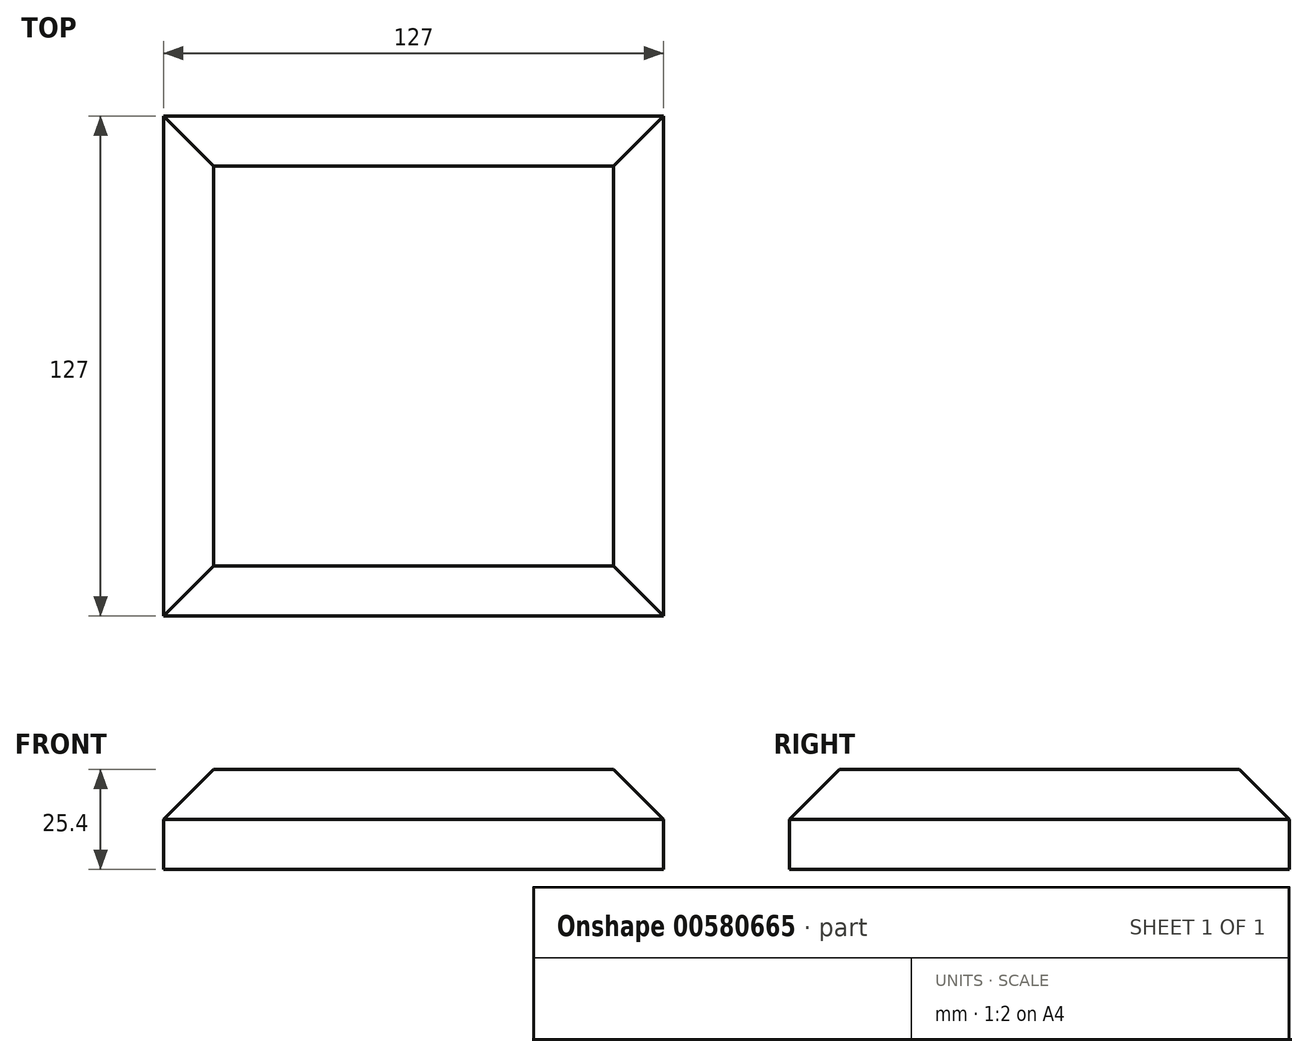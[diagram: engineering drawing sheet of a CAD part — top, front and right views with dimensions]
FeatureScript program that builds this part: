
annotation { "Feature Type Name" : "Feature", "Feature Type Description" : "" }
export const myFeature = defineFeature(function(context is Context, id is Id, definition is map)
    precondition{}
    {
        {
            var Q0;
            Q0=qCreatedBy(makeId("Top.planeOp"),FACE);
            var sketch = newSketch(context, id + "F0", { "sketchPlane" : qUnion([Q0])});
            skLineSegment(sketch, "E0.bottom", {"start": v(63.5, -63.5) * mm, "end": v(-63.5, -63.5) * mm});
            skLineSegment(sketch, "E0.top", {"start": v(63.5, 63.5) * mm, "end": v(-63.5, 63.5) * mm});
            skLineSegment(sketch, "E0.left", {"start": v(63.5, -63.5) * mm, "end": v(63.5, 63.5) * mm});
            skLineSegment(sketch, "E0.right", {"start": v(-63.5, -63.5) * mm, "end": v(-63.5, 63.5) * mm});
            skPoint(sketch, "E0.middle", {"position": v(0, 0) * mm});
            skSolve(sketch);
        }
        {
            var Q0;
            Q0=makeQuery(id+"F0.imprint","IMPRINT",FACE,{"disambiguationData":[TD([[makeQuery(id+"F0.imprint","IMPRINT",EDGE,{"derivedFrom":sQuery(id+"F0.wireOp",EDGE,"E0.bottom")}),-1.0]])]});
            extrude(context, id + "F1", {"entities" : qUnion([Q0]), "depth" : 25.4 * mm, "offsetDistance" : 25.4 * mm});
        }
        {
            var Q0;
            Q0=makeQuery(id+"F1.opExtrude","CAP_EDGE",EDGE,{"disambiguationData":[OSD([sQuery(id+"F0.wireOp",EDGE,"E0.bottom")])],"isStart":false});
            var Q1;
            Q1=makeQuery(id+"F1.opExtrude","CAP_EDGE",EDGE,{"disambiguationData":[OSD([sQuery(id+"F0.wireOp",EDGE,"E0.right")])],"isStart":false});
            var Q2;
            Q2=makeQuery(id+"F1.opExtrude","CAP_EDGE",EDGE,{"disambiguationData":[OSD([sQuery(id+"F0.wireOp",EDGE,"E0.left")])],"isStart":false});
            var Q3;
            Q3=makeQuery(id+"F1.opExtrude","CAP_EDGE",EDGE,{"disambiguationData":[OSD([sQuery(id+"F0.wireOp",EDGE,"E0.top")])],"isStart":false});
            chamfer(context, id + "F2", {"entities" : qUnion([Q0, Q1, Q2, Q3]), "width" : 12.7 * mm, "tangentPropagation" : true});
        }
    });
